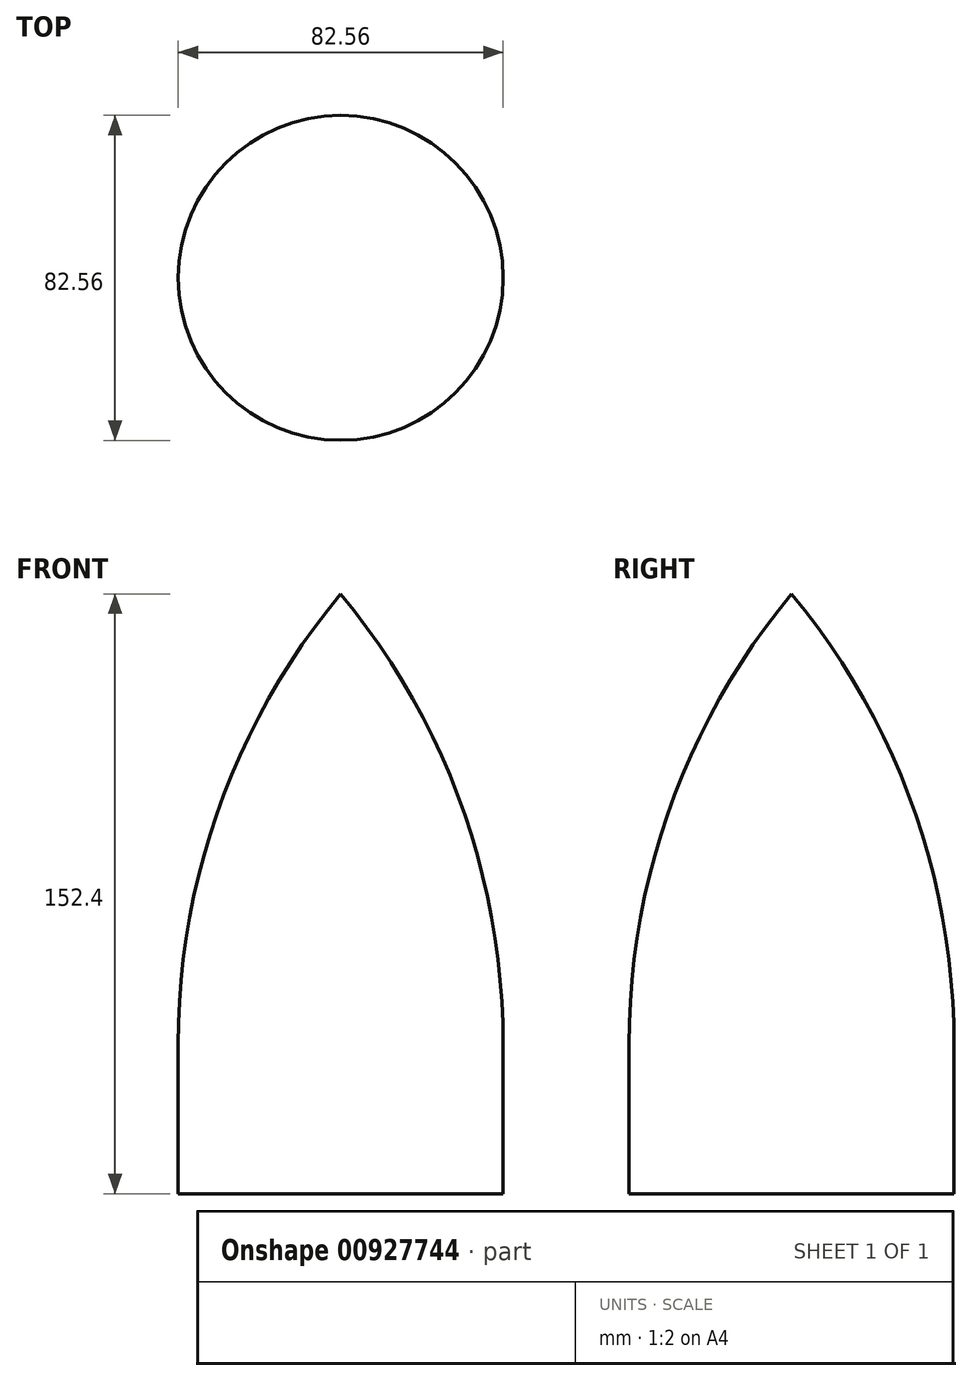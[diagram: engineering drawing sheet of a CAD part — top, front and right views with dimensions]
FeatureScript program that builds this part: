
annotation { "Feature Type Name" : "Feature", "Feature Type Description" : "" }
export const myFeature = defineFeature(function(context is Context, id is Id, definition is map)
    precondition{}
    {
        {
            var Q0;
            Q0=qCreatedBy(makeId("Front.planeOp"),FACE);
            var sketch = newSketch(context, id + "F0", { "sketchPlane" : qUnion([Q0])});
            skLineSegment(sketch, "E0", {"start": v(0, 0) * mm, "end": v(41.28, 0) * mm});
            skLineSegment(sketch, "E1", {"start": v(41.28, 0) * mm, "end": v(41.28, 37.96) * mm});
            skArc(sketch, "E2", {"start": v(41.28, 37.96) * mm, "mid": v(30.64, 98.79) * mm, "end": v(0, 152.4) * mm});
            skLineSegment(sketch, "E3", {"start": v(0, 152.4) * mm, "end": v(0, 0) * mm});
            skSolve(sketch);
        }
        {
            var Q0;
            Q0 = qSketchRegion(id + "F0", true);
            var Q1;
            Q1=sQuery(id+"F0.wireOp",EDGE,"E3");
            revolve(context, id + "F1", {"surfaceOperationType" : NewSurfaceOperationType.NEW, "entities" : qUnion([Q0]), "axis" : qUnion([Q1]), "revolveType" : RevolveType.FULL});
        }
    });
